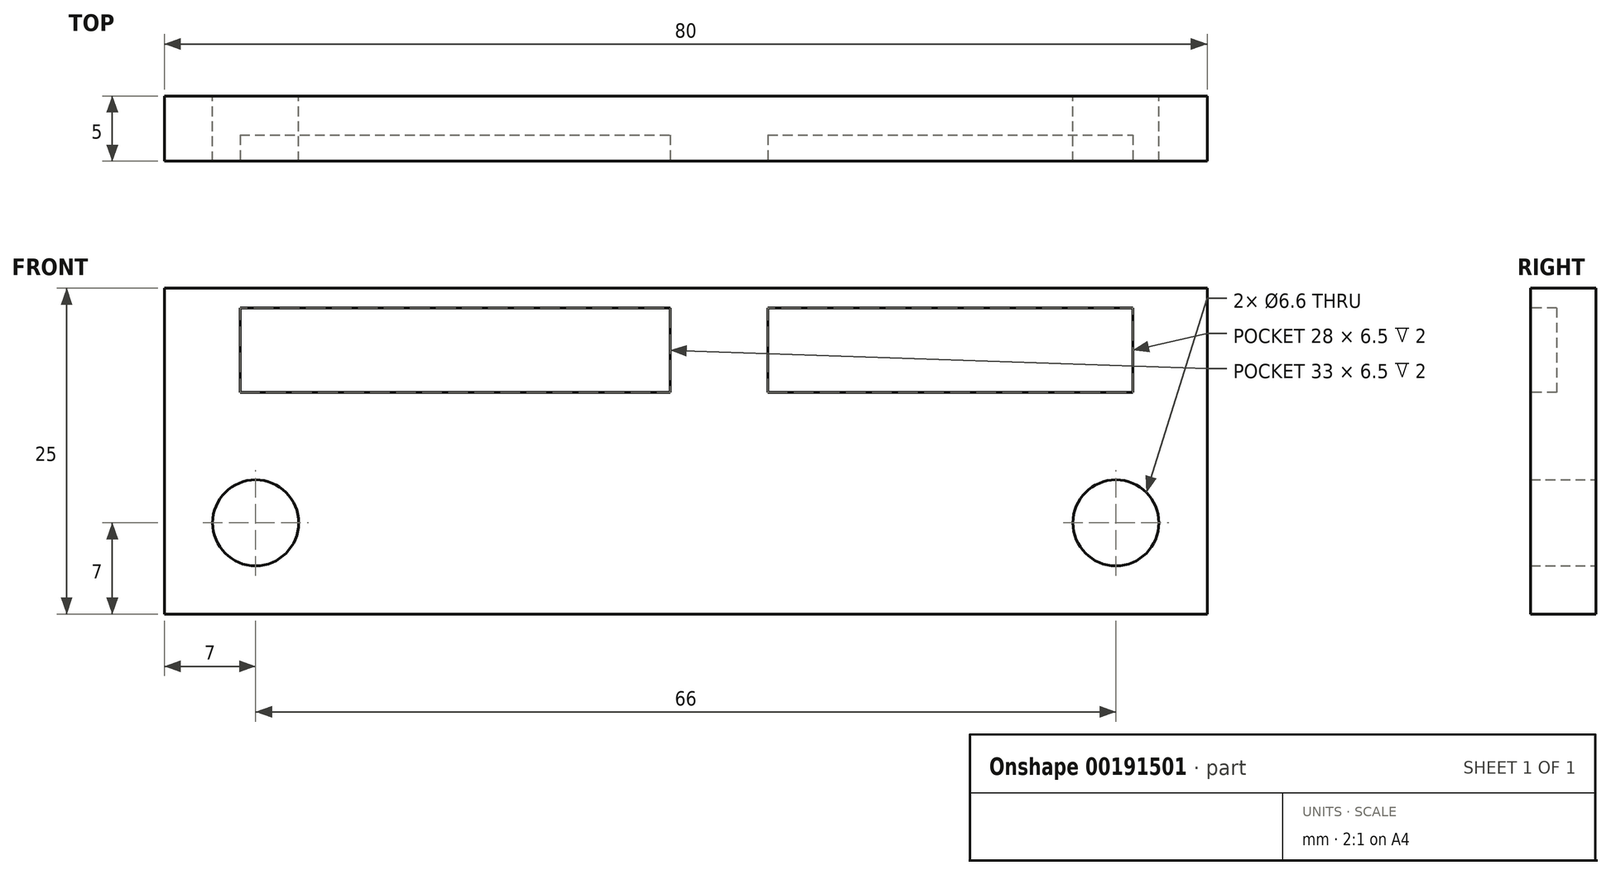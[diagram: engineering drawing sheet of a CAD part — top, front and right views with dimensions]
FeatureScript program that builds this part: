
annotation { "Feature Type Name" : "Feature", "Feature Type Description" : "" }
export const myFeature = defineFeature(function(context is Context, id is Id, definition is map)
    precondition{}
    {
        {
            var Q0;
            Q0=qCreatedBy(makeId("Front.planeOp"),FACE);
            var sketch = newSketch(context, id + "F0", { "sketchPlane" : qUnion([Q0])});
            skLineSegment(sketch, "E0.bottom", {"start": v(0, 0) * mm, "end": v(80, 0) * mm});
            skLineSegment(sketch, "E0.left", {"start": v(0, 0) * mm, "end": v(0, 17) * mm});
            skLineSegment(sketch, "E0.right", {"start": v(80, 0) * mm, "end": v(80, 17) * mm});
            skLineSegment(sketch, "E1.left", {"start": v(0, 17) * mm, "end": v(0, 23) * mm});
            skLineSegment(sketch, "E1.right", {"start": v(80, 17) * mm, "end": v(80, 23) * mm});
            skLineSegment(sketch, "E2.top", {"start": v(0, 25) * mm, "end": v(80, 25) * mm});
            skLineSegment(sketch, "E2.left", {"start": v(0, 23) * mm, "end": v(0, 25) * mm});
            skLineSegment(sketch, "E2.right", {"start": v(80, 23) * mm, "end": v(80, 25) * mm});
            skLineSegment(sketch, "E3.bottom", {"start": v(0, 0) * mm, "end": v(7, 0) * mm, "construction": true});
            skLineSegment(sketch, "E3.top", {"start": v(0, 7) * mm, "end": v(7, 7) * mm, "construction": true});
            skLineSegment(sketch, "E3.left", {"start": v(0, 0) * mm, "end": v(0, 7) * mm, "construction": true});
            skLineSegment(sketch, "E3.right", {"start": v(7, 0) * mm, "end": v(7, 7) * mm, "construction": true});
            skLineSegment(sketch, "E4.bottom", {"start": v(80, 0) * mm, "end": v(73, 0) * mm, "construction": true});
            skLineSegment(sketch, "E4.top", {"start": v(80, 7) * mm, "end": v(73, 7) * mm, "construction": true});
            skLineSegment(sketch, "E4.left", {"start": v(80, 0) * mm, "end": v(80, 7) * mm, "construction": true});
            skLineSegment(sketch, "E4.right", {"start": v(73, 0) * mm, "end": v(73, 7) * mm, "construction": true});
            skCircle(sketch, "E5", {"center": v(7, 7) * mm, "radius": 3.3 * mm});
            skCircle(sketch, "E6", {"center": v(73, 7) * mm, "radius": 3.3 * mm});
            skSolve(sketch);
        }
        {
            var Q0;
            Q0=makeQuery(id+"F0.imprint","IMPRINT",FACE,{"disambiguationData":[TD([[makeQuery(id+"F0.imprint","IMPRINT",EDGE,{"derivedFrom":sQuery(id+"F0.wireOp",EDGE,"E0.bottom")}),1.0]])]});
            var Q1;
            Q1=makeQuery(id+"F0.imprint","IMPRINT",FACE,{"disambiguationData":[TD([[makeQuery(id+"F0.imprint","IMPRINT",EDGE,{"derivedFrom":sQuery(id+"F0.wireOp",EDGE,"E2.bottom")}),1.0]])]});
            extrude(context, id + "F1", {"entities" : qUnion([Q0, Q1]), "depth" : 5 * mm});
        }
        {
            var Q0;
            Q0=makeQuery(id+"F1.opExtrude","CAP_FACE",FACE,{"disambiguationData":[OSD([sQuery(id+"F0.wireOp",EDGE,"E0.bottom"),sQuery(id+"F0.wireOp",EDGE,"E0.left"),sQuery(id+"F0.wireOp",EDGE,"E0.right"),sQuery(id+"F0.wireOp",EDGE,"E1.left"),sQuery(id+"F0.wireOp",EDGE,"E1.right"),sQuery(id+"F0.wireOp",EDGE,"E2.top"),sQuery(id+"F0.wireOp",EDGE,"E2.left"),sQuery(id+"F0.wireOp",EDGE,"E2.right"),sQuery(id+"F0.wireOp",EDGE,"E5"),sQuery(id+"F0.wireOp",EDGE,"E6")])],"isStart":false});
            var sketch = newSketch(context, id + "F2", { "sketchPlane" : qUnion([Q0])});
            skLineSegment(sketch, "E7", {"start": v(0, 25) * mm, "end": v(0, 23.5) * mm, "construction": true});
            skLineSegment(sketch, "E8", {"start": v(0, 23.5) * mm, "end": v(5.8, 23.5) * mm, "construction": true});
            skLineSegment(sketch, "E9.bottom", {"start": v(5.8, 23.5) * mm, "end": v(38.8, 23.5) * mm});
            skLineSegment(sketch, "E9.top", {"start": v(5.8, 17) * mm, "end": v(38.8, 17) * mm});
            skLineSegment(sketch, "E9.left", {"start": v(5.8, 23.5) * mm, "end": v(5.8, 17) * mm});
            skLineSegment(sketch, "E9.right", {"start": v(38.8, 23.5) * mm, "end": v(38.8, 17) * mm});
            skLineSegment(sketch, "E10", {"start": v(38.8, 23.5) * mm, "end": v(46.3, 23.5) * mm, "construction": true});
            skLineSegment(sketch, "E11.bottom", {"start": v(46.3, 23.5) * mm, "end": v(74.3, 23.5) * mm});
            skLineSegment(sketch, "E11.top", {"start": v(46.3, 17) * mm, "end": v(74.3, 17) * mm});
            skLineSegment(sketch, "E11.left", {"start": v(46.3, 23.5) * mm, "end": v(46.3, 17) * mm});
            skLineSegment(sketch, "E11.right", {"start": v(74.3, 23.5) * mm, "end": v(74.3, 17) * mm});
            skSolve(sketch);
        }
        {
            var Q0;
            Q0 = qSketchRegion(id + "F2", true);
            extrude(context, id + "F3", {"entities" : qUnion([Q0]), "operationType" : NewBodyOperationType.REMOVE, "oppositeDirection" : true, "depth" : 2 * mm});
        }
    });
